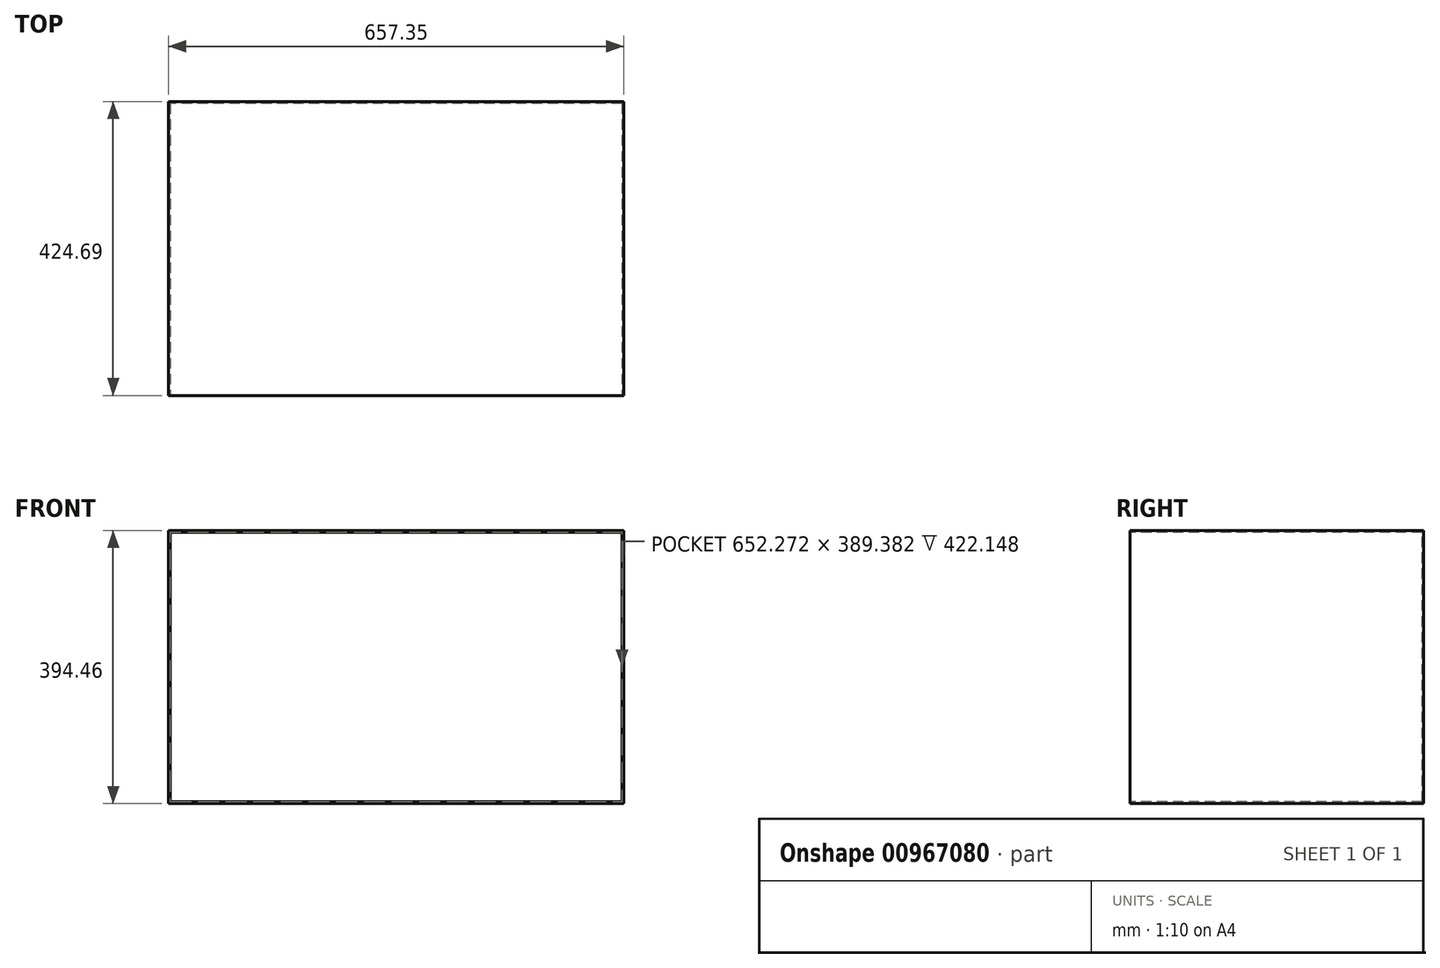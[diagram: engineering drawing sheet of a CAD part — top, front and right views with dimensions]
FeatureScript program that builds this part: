
annotation { "Feature Type Name" : "Feature", "Feature Type Description" : "" }
export const myFeature = defineFeature(function(context is Context, id is Id, definition is map)
    precondition{}
    {
        {
            var Q0;
            Q0=qCreatedBy(makeId("Front.planeOp"),FACE);
            var sketch = newSketch(context, id + "F0", { "sketchPlane" : qUnion([Q0])});
            skLineSegment(sketch, "E0.bottom", {"start": v(0, 0) * mm, "end": v(-657.35, 0) * mm});
            skLineSegment(sketch, "E0.top", {"start": v(0, 394.46) * mm, "end": v(-657.35, 394.46) * mm});
            skLineSegment(sketch, "E0.left", {"start": v(0, 0) * mm, "end": v(0, 394.46) * mm});
            skLineSegment(sketch, "E0.right", {"start": v(-657.35, 0) * mm, "end": v(-657.35, 394.46) * mm});
            skSolve(sketch);
        }
        {
            var Q0;
            Q0=makeQuery(id+"F0.imprint","IMPRINT",FACE,{"disambiguationData":[TD([[makeQuery(id+"F0.imprint","IMPRINT",EDGE,{"derivedFrom":sQuery(id+"F0.wireOp",EDGE,"E0.bottom")}),-1.0]])]});
            extrude(context, id + "F1", {"entities" : qUnion([Q0]), "oppositeDirection" : true, "depth" : 424.7 * mm, "offsetDistance" : 25.4 * mm});
        }
        {
            var Q0;
            Q0=makeQuery(id+"F1.opExtrude","CAP_FACE",FACE,{"disambiguationData":[OSD([sQuery(id+"F0.wireOp",EDGE,"E0.bottom"),sQuery(id+"F0.wireOp",EDGE,"E0.top"),sQuery(id+"F0.wireOp",EDGE,"E0.left"),sQuery(id+"F0.wireOp",EDGE,"E0.right")])],"isStart":true});
            shell(context, id + "F2", {"entities" : qUnion([Q0]), "thickness" : 2.54 * mm});
        }
    });
